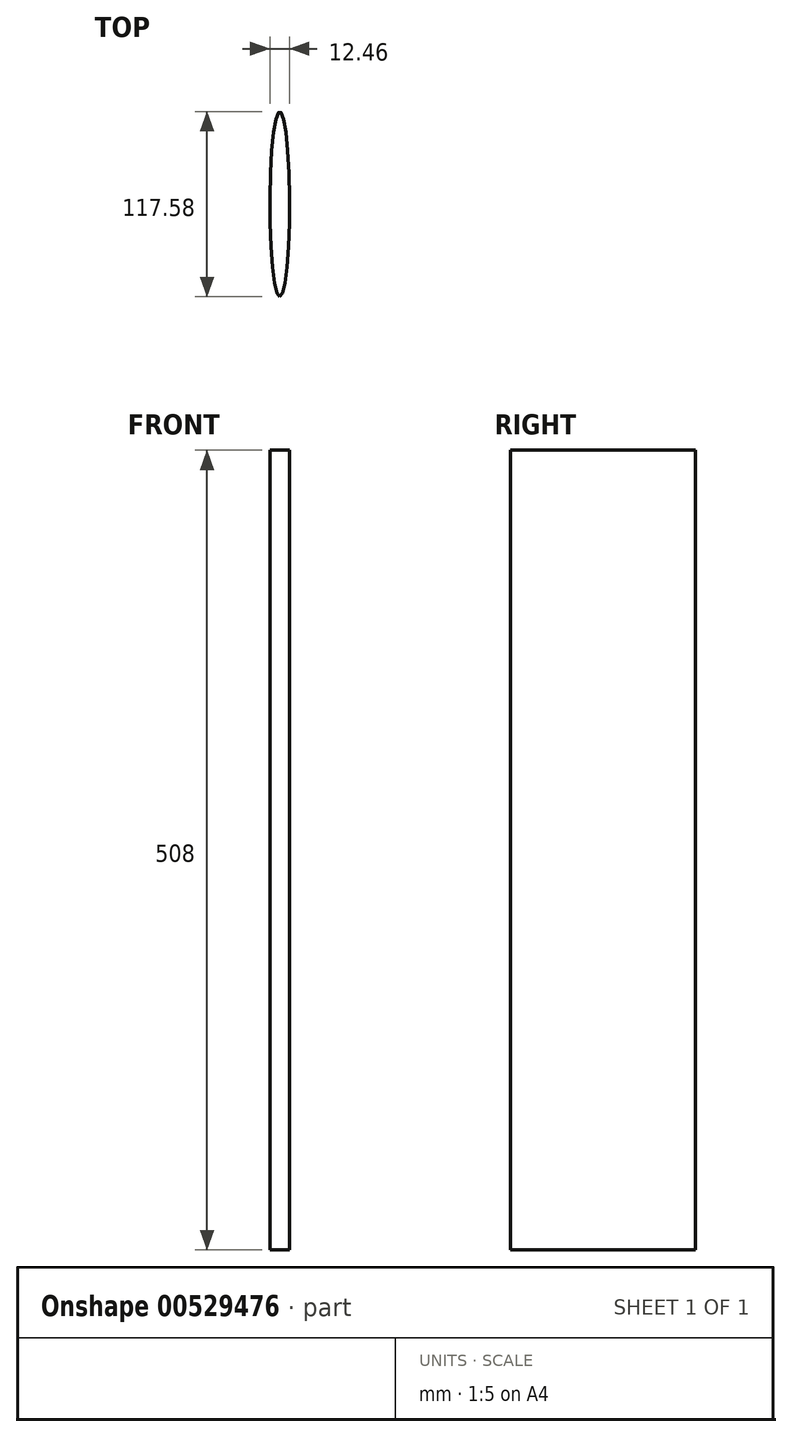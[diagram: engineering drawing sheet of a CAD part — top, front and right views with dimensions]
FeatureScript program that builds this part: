
annotation { "Feature Type Name" : "Feature", "Feature Type Description" : "" }
export const myFeature = defineFeature(function(context is Context, id is Id, definition is map)
    precondition{}
    {
        {
            var Q0;
            Q0=qCreatedBy(makeId("Top.planeOp"),FACE);
            var sketch = newSketch(context, id + "F0", { "sketchPlane" : qUnion([Q0])});
            skEllipse(sketch, "E0", {"center": v(0, 0) * mm, "majorRadius": 58.8 * mm, "minorRadius": 6.23 * mm, "majorAxis": v(0, -1)});
            skSolve(sketch);
        }
        {
            var Q0;
            Q0=sQuery(id+"F0.wireOp",EDGE,"E0");
            extrude(context, id + "F1", {"bodyType" : ToolBodyType.SURFACE, "surfaceEntities" : qUnion([Q0]), "depth" : 508 * mm, "offsetDistance" : 25.4 * mm});
        }
    });
